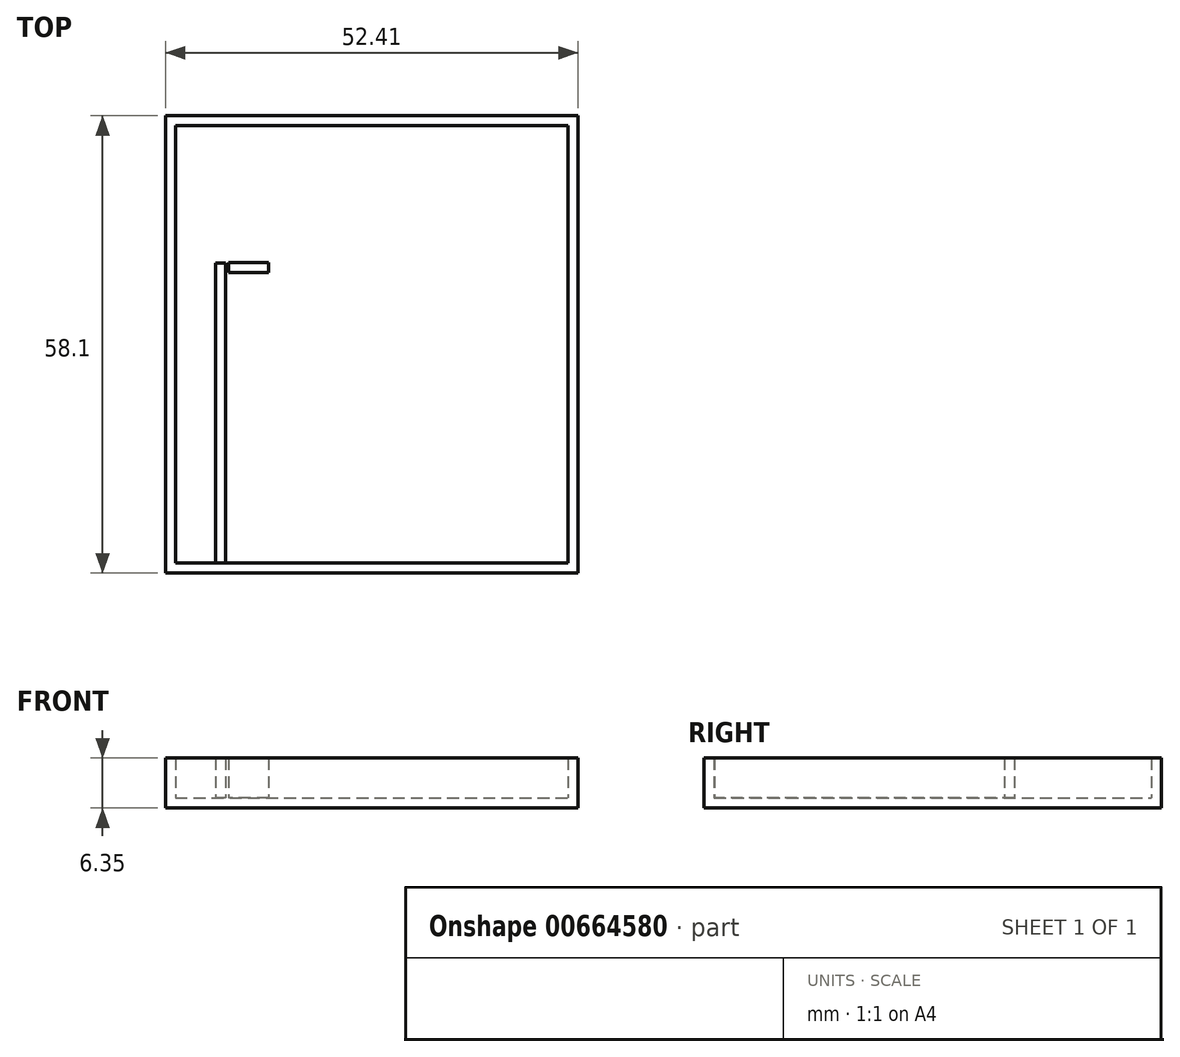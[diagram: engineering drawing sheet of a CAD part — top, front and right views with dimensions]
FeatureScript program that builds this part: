
annotation { "Feature Type Name" : "Feature", "Feature Type Description" : "" }
export const myFeature = defineFeature(function(context is Context, id is Id, definition is map)
    precondition{}
    {
        {
            var Q0;
            Q0=qCreatedBy(makeId("Top.planeOp"),FACE);
            var sketch = newSketch(context, id + "F0", { "sketchPlane" : qUnion([Q0])});
            skLineSegment(sketch, "E0.bottom", {"start": v(0, 0) * mm, "end": v(52.41, 0) * mm});
            skLineSegment(sketch, "E0.top", {"start": v(0, 58.1) * mm, "end": v(52.41, 58.1) * mm});
            skLineSegment(sketch, "E0.left", {"start": v(0, 0) * mm, "end": v(0, 58.1) * mm});
            skLineSegment(sketch, "E0.right", {"start": v(52.41, 0) * mm, "end": v(52.41, 58.1) * mm});
            skSolve(sketch);
        }
        {
            var Q0;
            Q0=makeQuery(id+"F0.imprint","IMPRINT",FACE,{"disambiguationData":[TD([[makeQuery(id+"F0.imprint","IMPRINT",EDGE,{"derivedFrom":sQuery(id+"F0.wireOp",EDGE,"E0.bottom")}),1.0]])]});
            extrude(context, id + "F1", {"entities" : qUnion([Q0]), "depth" : 6.35 * mm, "offsetDistance" : 25.4 * mm});
        }
        {
            var Q0;
            Q0=makeQuery(id+"F1.opExtrude","CAP_FACE",FACE,{"disambiguationData":[OSD([sQuery(id+"F0.wireOp",EDGE,"E0.bottom"),sQuery(id+"F0.wireOp",EDGE,"E0.top"),sQuery(id+"F0.wireOp",EDGE,"E0.left"),sQuery(id+"F0.wireOp",EDGE,"E0.right")])],"isStart":false});
            shell(context, id + "F2", {"entities" : qUnion([Q0]), "thickness" : 1.27 * mm});
        }
        {
            var Q0;
            Q0=qCreatedBy(makeId("Top.planeOp"),FACE);
            var sketch = newSketch(context, id + "F3", { "sketchPlane" : qUnion([Q0])});
            skLineSegment(sketch, "E1.bottom", {"start": v(1.25, 1.3) * mm, "end": v(6.33, 1.3) * mm});
            skLineSegment(sketch, "E1.top", {"start": v(1.25, 1.3) * mm, "end": v(6.33, 1.3) * mm});
            skLineSegment(sketch, "E1.left", {"start": v(1.25, 1.3) * mm, "end": v(1.25, 1.3) * mm});
            skLineSegment(sketch, "E1.right", {"start": v(6.33, 1.3) * mm, "end": v(6.33, 1.3) * mm});
            skLineSegment(sketch, "E2.bottom", {"start": v(6.33, 1.3) * mm, "end": v(7.6, 1.3) * mm});
            skLineSegment(sketch, "E2.top", {"start": v(6.33, 39.4) * mm, "end": v(7.6, 39.4) * mm});
            skLineSegment(sketch, "E2.left", {"start": v(6.33, 1.3) * mm, "end": v(6.33, 39.4) * mm});
            skLineSegment(sketch, "E2.right", {"start": v(7.6, 1.3) * mm, "end": v(7.6, 39.4) * mm});
            skSolve(sketch);
        }
        {
            var Q0;
            Q0 = qSketchRegion(id + "F3", true);
            extrude(context, id + "F4", {"entities" : qUnion([Q0]), "operationType" : NewBodyOperationType.ADD, "depth" : 6.35 * mm, "offsetDistance" : 25.4 * mm});
        }
        {
            var Q0;
            Q0=qCreatedBy(makeId("Top.planeOp"),FACE);
            var sketch = newSketch(context, id + "F5", { "sketchPlane" : qUnion([Q0])});
            skLineSegment(sketch, "E3.bottom", {"start": v(8.02, 39.44) * mm, "end": v(13.1, 39.44) * mm});
            skLineSegment(sketch, "E3.top", {"start": v(8.02, 38.17) * mm, "end": v(13.1, 38.17) * mm});
            skLineSegment(sketch, "E3.left", {"start": v(8.02, 39.44) * mm, "end": v(8.02, 38.17) * mm});
            skLineSegment(sketch, "E3.right", {"start": v(13.1, 39.44) * mm, "end": v(13.1, 38.17) * mm});
            skSolve(sketch);
        }
        {
            var Q0;
            Q0 = qSketchRegion(id + "F5", true);
            extrude(context, id + "F6", {"entities" : qUnion([Q0]), "operationType" : NewBodyOperationType.ADD, "depth" : 6.35 * mm, "offsetDistance" : 25.4 * mm});
        }
    });
